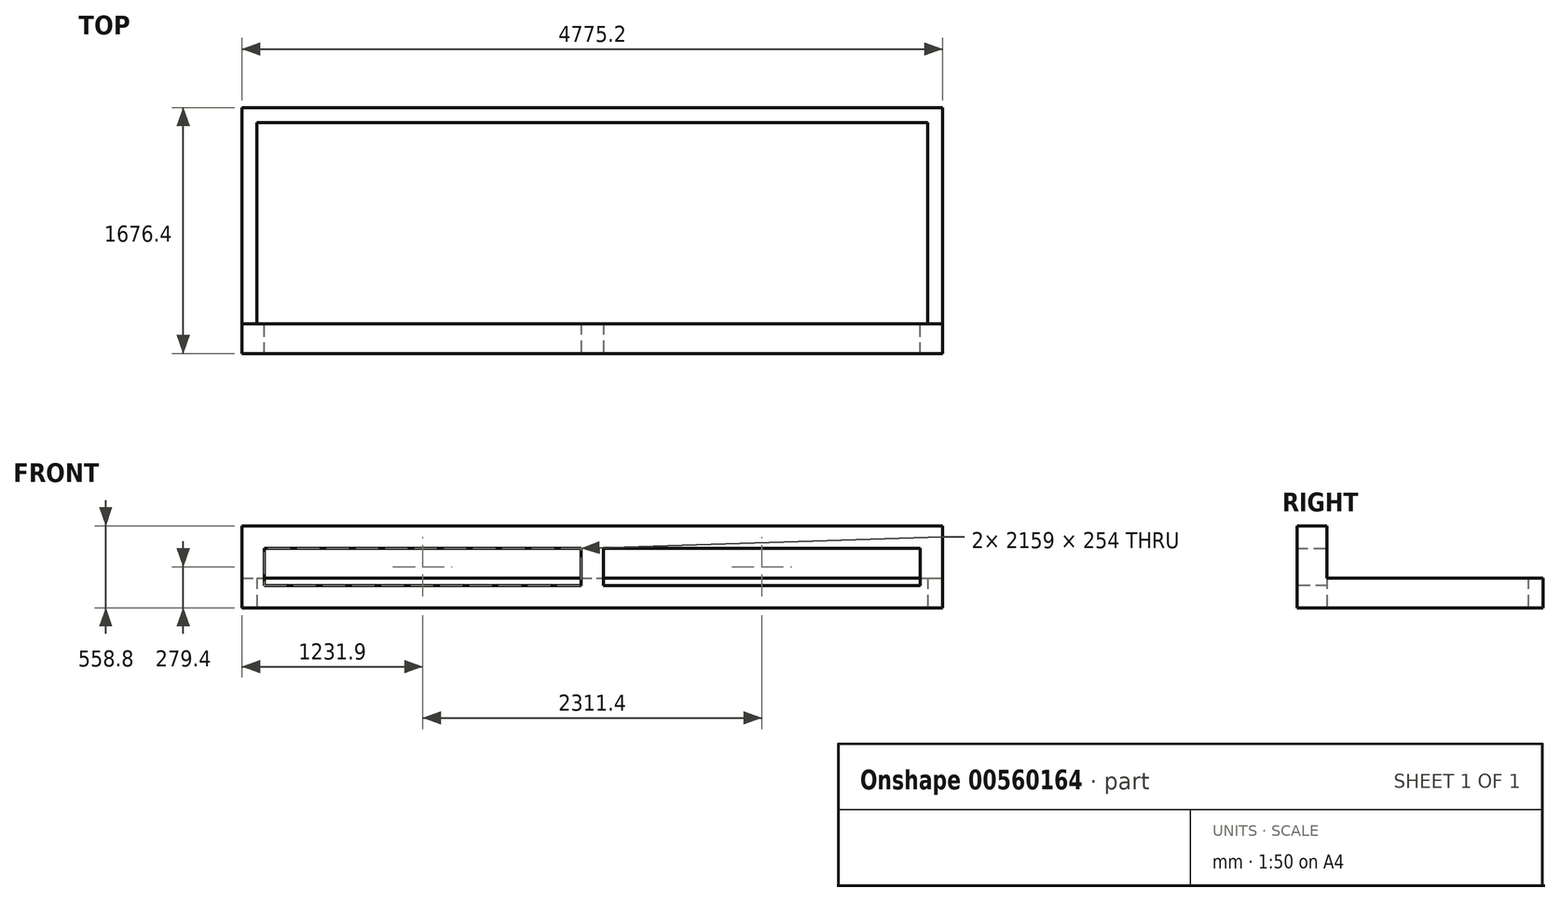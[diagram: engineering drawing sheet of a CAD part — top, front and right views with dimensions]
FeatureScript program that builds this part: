
annotation { "Feature Type Name" : "Feature", "Feature Type Description" : "" }
export const myFeature = defineFeature(function(context is Context, id is Id, definition is map)
    precondition{}
    {
        {
            var Q0;
            Q0=qCreatedBy(makeId("Top.planeOp"),FACE);
            var sketch = newSketch(context, id + "F0", { "sketchPlane" : qUnion([Q0])});
            skLineSegment(sketch, "E0.bottom", {"start": v(-2387.6, 787.4) * mm, "end": v(2387.6, 787.4) * mm});
            skLineSegment(sketch, "E0.top", {"start": v(-2387.6, -889) * mm, "end": v(2387.6, -889) * mm});
            skLineSegment(sketch, "E0.left", {"start": v(-2387.6, 787.4) * mm, "end": v(-2387.6, -889) * mm});
            skLineSegment(sketch, "E0.right", {"start": v(2387.6, 787.4) * mm, "end": v(2387.6, -889) * mm});
            skLineSegment(sketch, "E1.bottom", {"start": v(-2286, 685.8) * mm, "end": v(2286, 685.8) * mm});
            skLineSegment(sketch, "E1.top", {"start": v(-2286, -685.8) * mm, "end": v(2286, -685.8) * mm});
            skLineSegment(sketch, "E1.left", {"start": v(-2286, 685.8) * mm, "end": v(-2286, -685.8) * mm});
            skLineSegment(sketch, "E1.right", {"start": v(2286, 685.8) * mm, "end": v(2286, -685.8) * mm});
            skSolve(sketch);
        }
        {
            var Q0;
            Q0=qSketchRegion(id+"F0",true);
            extrude(context, id + "F1", {"entities" : qUnion([Q0]), "depth" : 203.2 * mm, "offsetDistance" : 25.4 * mm});
        }
        {
            var Q0;
            Q0=makeQuery(id+"F1.opExtrude","CAP_FACE",FACE,{"disambiguationData":[OSD([sQuery(id+"F0.wireOp",EDGE,"E0.bottom"),sQuery(id+"F0.wireOp",EDGE,"E0.top"),sQuery(id+"F0.wireOp",EDGE,"E0.left"),sQuery(id+"F0.wireOp",EDGE,"E0.right"),sQuery(id+"F0.wireOp",EDGE,"E1.bottom"),sQuery(id+"F0.wireOp",EDGE,"E1.top"),sQuery(id+"F0.wireOp",EDGE,"E1.left"),sQuery(id+"F0.wireOp",EDGE,"E1.right")])],"isStart":false});
            var sketch = newSketch(context, id + "F2", { "sketchPlane" : qUnion([Q0])});
            skLineSegment(sketch, "E2.bottom", {"start": v(2387.6, -889) * mm, "end": v(-2387.6, -889) * mm});
            skLineSegment(sketch, "E2.top", {"start": v(2387.6, -685.8) * mm, "end": v(-2387.6, -685.8) * mm});
            skLineSegment(sketch, "E2.left", {"start": v(2387.6, -889) * mm, "end": v(2387.6, -685.8) * mm});
            skLineSegment(sketch, "E2.right", {"start": v(-2387.6, -889) * mm, "end": v(-2387.6, -685.8) * mm});
            skSolve(sketch);
        }
        {
            var Q0;
            Q0=qSketchRegion(id+"F2",true);
            extrude(context, id + "F3", {"entities" : qUnion([Q0]), "operationType" : NewBodyOperationType.REMOVE, "oppositeDirection" : true, "depth" : 50.8 * mm, "offsetDistance" : 25.4 * mm});
        }
        {
            var Q0;
            Q0=makeQuery(id+"F3.boolean.opBoolean","COPY",FACE,{"derivedFrom":makeQuery(id+"F3.opExtrude","CAP_FACE",FACE,{"disambiguationData":[OSD([sQuery(id+"F2.wireOp",EDGE,"E2.bottom"),sQuery(id+"F2.wireOp",EDGE,"E2.top"),sQuery(id+"F2.wireOp",EDGE,"E2.left"),sQuery(id+"F2.wireOp",EDGE,"E2.right")])],"isStart":false})});
            var sketch = newSketch(context, id + "F4", { "sketchPlane" : qUnion([Q0])});
            skLineSegment(sketch, "E3.bottom", {"start": v(-2387.6, -889) * mm, "end": v(-2235.2, -889) * mm});
            skLineSegment(sketch, "E3.top", {"start": v(-2387.6, -685.8) * mm, "end": v(-2235.2, -685.8) * mm});
            skLineSegment(sketch, "E3.left", {"start": v(-2387.6, -889) * mm, "end": v(-2387.6, -685.8) * mm});
            skLineSegment(sketch, "E3.right", {"start": v(-2235.2, -889) * mm, "end": v(-2235.2, -685.8) * mm});
            skLineSegment(sketch, "E4.bottom", {"start": v(2387.6, -889) * mm, "end": v(2235.2, -889) * mm});
            skLineSegment(sketch, "E4.top", {"start": v(2387.6, -685.8) * mm, "end": v(2235.2, -685.8) * mm});
            skLineSegment(sketch, "E4.left", {"start": v(2387.6, -889) * mm, "end": v(2387.6, -685.8) * mm});
            skLineSegment(sketch, "E4.right", {"start": v(2235.2, -889) * mm, "end": v(2235.2, -685.8) * mm});
            skLineSegment(sketch, "E5.bottom", {"start": v(-76.2, -685.8) * mm, "end": v(76.2, -685.8) * mm});
            skLineSegment(sketch, "E5.top", {"start": v(-76.2, -889) * mm, "end": v(76.2, -889) * mm});
            skLineSegment(sketch, "E5.left", {"start": v(-76.2, -685.8) * mm, "end": v(-76.2, -889) * mm});
            skLineSegment(sketch, "E5.right", {"start": v(76.2, -685.8) * mm, "end": v(76.2, -889) * mm});
            skSolve(sketch);
        }
        {
            var Q0;
            Q0=qSketchRegion(id+"F4",true);
            extrude(context, id + "F5", {"entities" : qUnion([Q0]), "operationType" : NewBodyOperationType.ADD, "depth" : 254 * mm, "offsetDistance" : 25.4 * mm});
        }
        {
            var Q0;
            Q0=makeQuery(id+"F5.opExtrude","CAP_FACE",FACE,{"disambiguationData":[OSD([sQuery(id+"F4.wireOp",EDGE,"E3.bottom"),sQuery(id+"F4.wireOp",EDGE,"E3.top"),sQuery(id+"F4.wireOp",EDGE,"E3.left"),sQuery(id+"F4.wireOp",EDGE,"E3.right")])],"isStart":false});
            var sketch = newSketch(context, id + "F6", { "sketchPlane" : qUnion([Q0])});
            skLineSegment(sketch, "E6.bottom", {"start": v(-2387.6, -685.8) * mm, "end": v(2387.6, -685.8) * mm});
            skLineSegment(sketch, "E6.top", {"start": v(-2387.6, -889) * mm, "end": v(2387.6, -889) * mm});
            skLineSegment(sketch, "E6.left", {"start": v(-2387.6, -685.8) * mm, "end": v(-2387.6, -889) * mm});
            skLineSegment(sketch, "E6.right", {"start": v(2387.6, -685.8) * mm, "end": v(2387.6, -889) * mm});
            skSolve(sketch);
        }
        {
            var Q0;
            Q0=qSketchRegion(id+"F6",true);
            extrude(context, id + "F7", {"entities" : qUnion([Q0]), "operationType" : NewBodyOperationType.ADD, "depth" : 152.4 * mm, "offsetDistance" : 25.4 * mm});
        }
    });
